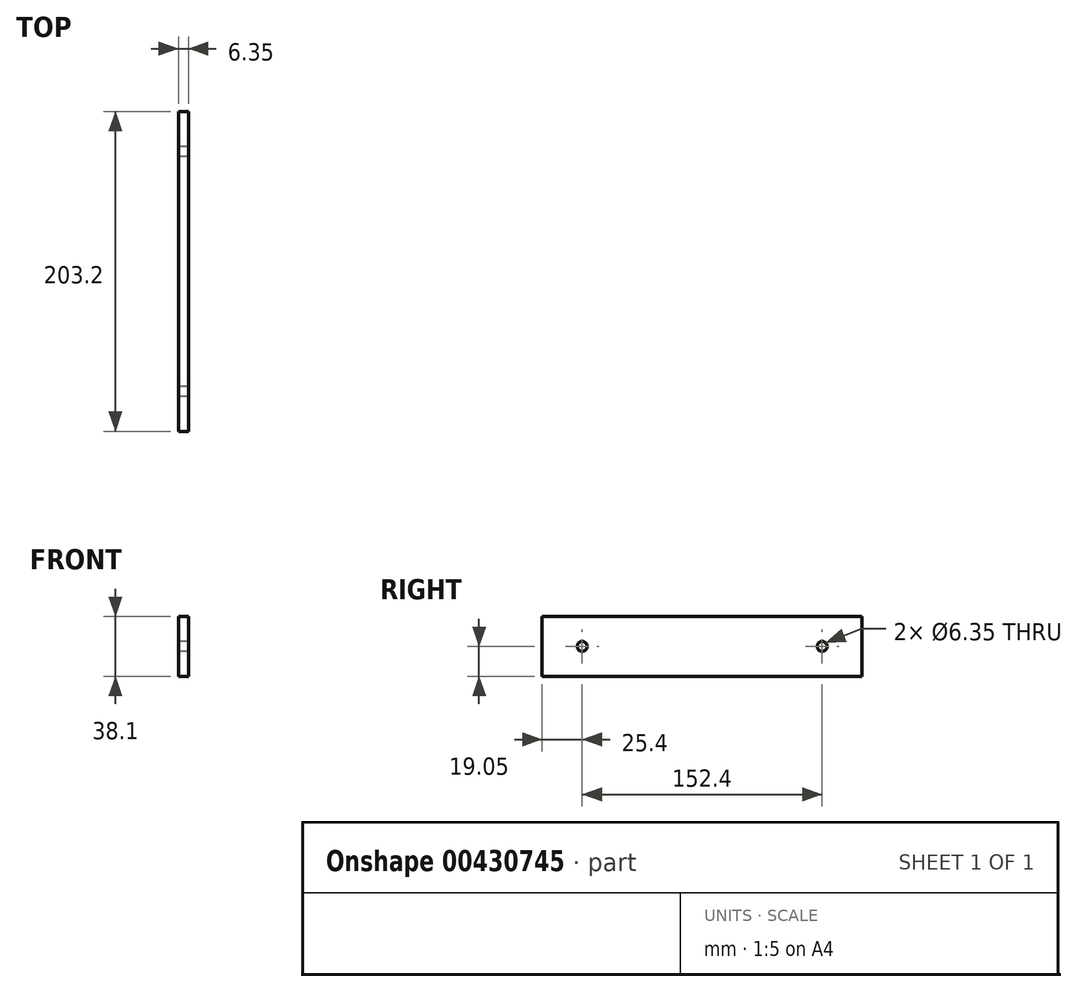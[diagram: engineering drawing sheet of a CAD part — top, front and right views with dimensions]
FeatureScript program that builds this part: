
annotation { "Feature Type Name" : "Feature", "Feature Type Description" : "" }
export const myFeature = defineFeature(function(context is Context, id is Id, definition is map)
    precondition{}
    {
        {
            var Q0;
            Q0=qCreatedBy(makeId("Right.planeOp"),FACE);
            var sketch = newSketch(context, id + "F0", { "sketchPlane" : qUnion([Q0])});
            skLineSegment(sketch, "E0.bottom", {"start": v(0, 0) * mm, "end": v(203.2, 0) * mm});
            skLineSegment(sketch, "E0.top", {"start": v(0, 38.1) * mm, "end": v(203.2, 38.1) * mm});
            skLineSegment(sketch, "E0.left", {"start": v(0, 0) * mm, "end": v(0, 38.1) * mm});
            skLineSegment(sketch, "E0.right", {"start": v(203.2, 0) * mm, "end": v(203.2, 38.1) * mm});
            skLineSegment(sketch, "E1", {"start": v(0, 19.05) * mm, "end": v(203.2, 19.05) * mm, "construction": true});
            skLineSegment(sketch, "E2", {"start": v(101.6, 38.1) * mm, "end": v(101.6, 0) * mm, "construction": true});
            skCircle(sketch, "E3", {"center": v(177.8, 19.05) * mm, "radius": 3.18 * mm});
            skCircle(sketch, "E4", {"center": v(25.4, 19.05) * mm, "radius": 3.18 * mm});
            skSolve(sketch);
        }
        {
            var Q0;
            Q0=makeQuery(id+"F0.imprint","IMPRINT",FACE,{"disambiguationData":[TD([[makeQuery(id+"F0.imprint","IMPRINT",EDGE,{"derivedFrom":sQuery(id+"F0.wireOp",EDGE,"E0.bottom")}),1.0]])]});
            extrude(context, id + "F1", {"entities" : qUnion([Q0]), "depth" : 6.35 * mm, "offsetDistance" : 25.4 * mm});
        }
    });
